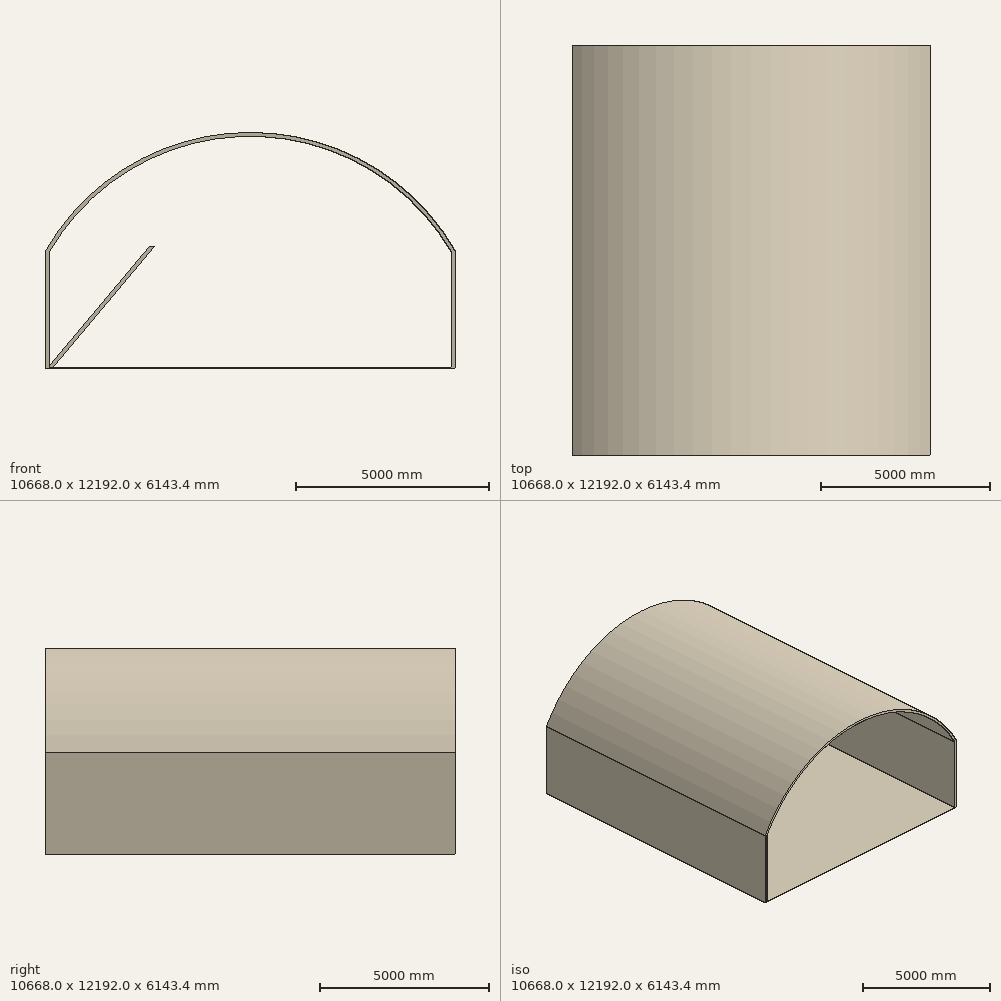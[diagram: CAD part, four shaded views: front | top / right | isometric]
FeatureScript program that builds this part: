
annotation { "Feature Type Name" : "Feature", "Feature Type Description" : "" }
export const myFeature = defineFeature(function(context is Context, id is Id, definition is map)
    precondition{}
    {
        {
            var Q0;
            Q0=qCreatedBy(makeId("Front.planeOp"),FACE);
            var sketch = newSketch(context, id + "F0", { "sketchPlane" : qUnion([Q0])});
            skLineSegment(sketch, "E0", {"start": v(-5334, 0) * mm, "end": v(5334, 0) * mm});
            skLineSegment(sketch, "E1", {"start": v(-5334, 0) * mm, "end": v(-5334, 3048) * mm});
            skLineSegment(sketch, "E2", {"start": v(5334, 0) * mm, "end": v(5334, 3048) * mm});
            skArc(sketch, "E3", {"start": v(5334, 3048) * mm, "mid": v(0, 6143.44) * mm, "end": v(-5334, 3048) * mm});
            skLineSegment(sketch, "E4", {"start": v(-5232.4, 25.4) * mm, "end": v(5232.4, 25.4) * mm});
            skLineSegment(sketch, "E5", {"start": v(5232.4, 25.4) * mm, "end": v(5232.4, 3020.9) * mm});
            skLineSegment(sketch, "E6", {"start": v(-5232.4, 25.4) * mm, "end": v(-5232.4, 3020.9) * mm});
            skArc(sketch, "E7", {"start": v(5232.4, 3020.9) * mm, "mid": v(0, 6041.84) * mm, "end": v(-5232.4, 3020.9) * mm});
            skSolve(sketch);
        }
        {
            var Q0;
            Q0 = qSketchRegion(id + "F0", true);
            extrude(context, id + "F1", {"entities" : qUnion([Q0]), "oppositeDirection" : true, "depth" : 12192 * mm, "offsetDistance" : 25.4 * mm});
        }
        {
            var Q0;
            Q0=makeQuery(id+"F1.opExtrude","CAP_FACE",FACE,{"disambiguationData":[OSD([sQuery(id+"F0.wireOp",EDGE,"E0"),sQuery(id+"F0.wireOp",EDGE,"E1"),sQuery(id+"F0.wireOp",EDGE,"E2"),sQuery(id+"F0.wireOp",EDGE,"E3"),sQuery(id+"F0.wireOp",EDGE,"E4"),sQuery(id+"F0.wireOp",EDGE,"E5"),sQuery(id+"F0.wireOp",EDGE,"E6"),sQuery(id+"F0.wireOp",EDGE,"E7")])],"isStart":true});
            cPlane(context, id + "F2", {"entities" : qUnion([Q0]), "cplaneType" : CPlaneType.OFFSET, "offset" : 3048 * mm, "oppositeDirection" : true, "width" : 152.4 * mm, "height" : 152.4 * mm});
        }
        {
            var Q0;
            Q0=qCreatedBy(id+"F2.planeOp",FACE);
            var sketch = newSketch(context, id + "F3", { "sketchPlane" : qUnion([Q0])});
            skLineSegment(sketch, "E8", {"start": v(-5232.4, 62.38) * mm, "end": v(-2629.13, 3164.84) * mm});
            skLineSegment(sketch, "E9", {"start": v(-2629.13, 3164.84) * mm, "end": v(-2496.5, 3164.84) * mm});
            skLineSegment(sketch, "E10", {"start": v(-2496.5, 3164.84) * mm, "end": v(-5130.8, 25.4) * mm});
            skLineSegment(sketch, "E11", {"start": v(-5130.8, 25.4) * mm, "end": v(-5232.4, 25.4) * mm});
            skLineSegment(sketch, "E12", {"start": v(-5232.4, 25.4) * mm, "end": v(-5232.4, 62.38) * mm});
            skSolve(sketch);
        }
        {
            var Q0;
            Q0 = qSketchRegion(id + "F3", true);
            extrude(context, id + "F4", {"entities" : qUnion([Q0]), "endBound" : BoundingType.SYMMETRIC, "depth" : 1828.8 * mm, "offsetDistance" : 25.4 * mm});
        }
    });
